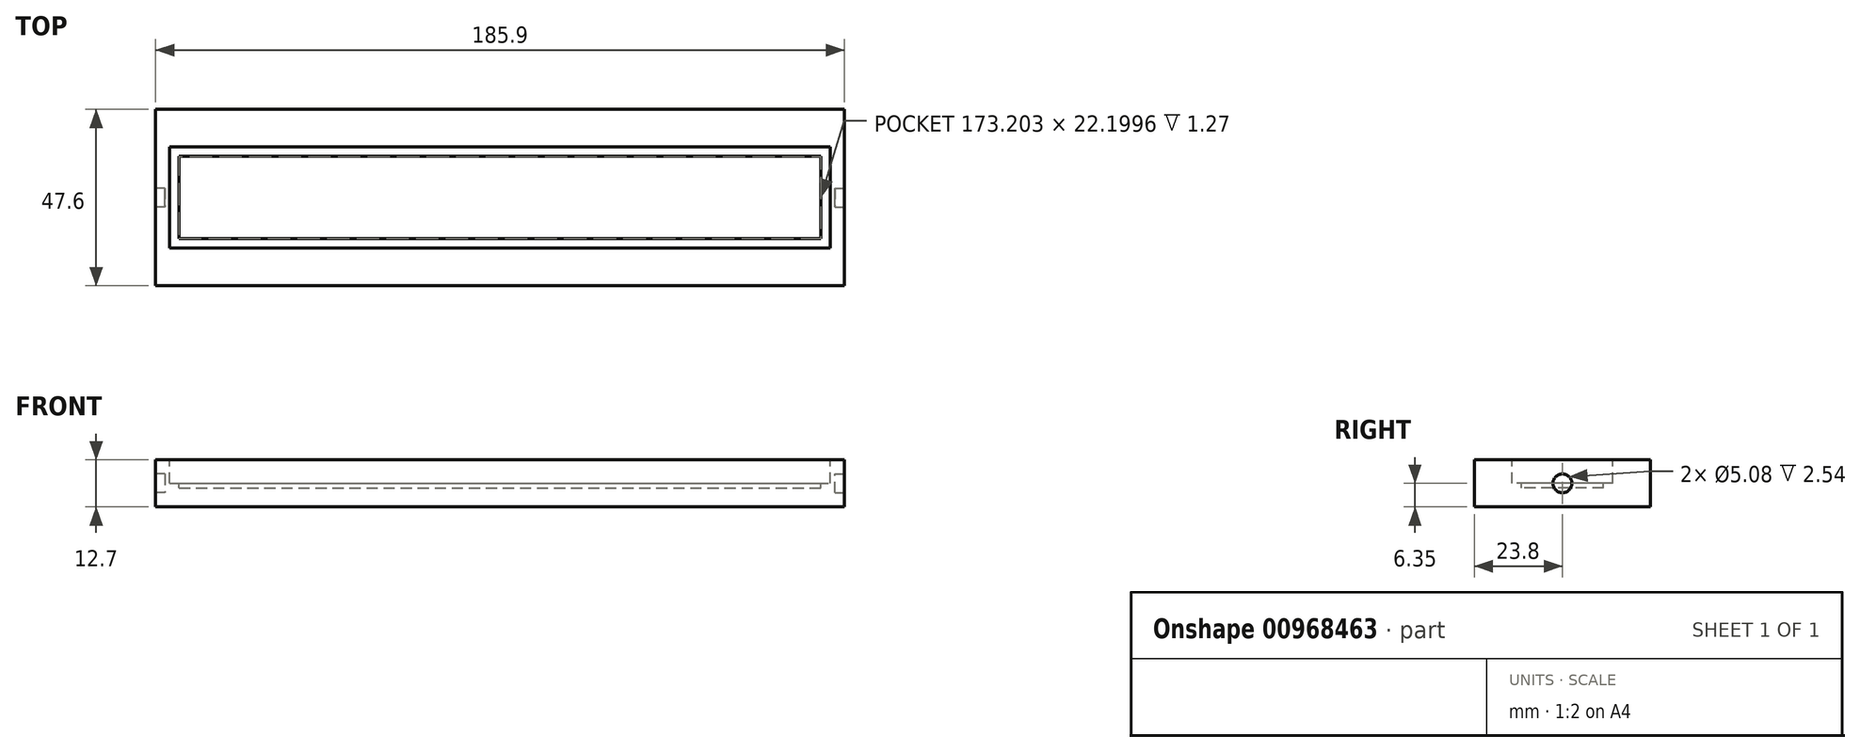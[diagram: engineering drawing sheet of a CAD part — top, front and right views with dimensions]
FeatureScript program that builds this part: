
annotation { "Feature Type Name" : "Feature", "Feature Type Description" : "" }
export const myFeature = defineFeature(function(context is Context, id is Id, definition is map)
    precondition{}
    {
        {
            var Q0;
            Q0=qCreatedBy(makeId("Top.planeOp"),FACE);
            var sketch = newSketch(context, id + "F0", { "sketchPlane" : qUnion([Q0])});
            skLineSegment(sketch, "E0.bottom", {"start": v(-92.95, 23.8) * mm, "end": v(92.95, 23.8) * mm});
            skLineSegment(sketch, "E0.top", {"start": v(-92.95, -23.8) * mm, "end": v(92.95, -23.8) * mm});
            skLineSegment(sketch, "E0.left", {"start": v(-92.95, 23.8) * mm, "end": v(-92.95, -23.8) * mm});
            skLineSegment(sketch, "E0.right", {"start": v(92.95, 23.8) * mm, "end": v(92.95, -23.8) * mm});
            skPoint(sketch, "E0.middle", {"position": v(0, 0) * mm});
            skSolve(sketch);
        }
        {
            var Q0;
            Q0=makeQuery(id+"F0.imprint","IMPRINT",FACE,{"disambiguationData":[TD([[makeQuery(id+"F0.imprint","IMPRINT",EDGE,{"derivedFrom":sQuery(id+"F0.wireOp",EDGE,"E0.bottom")}),-1.0]])]});
            extrude(context, id + "F1", {"entities" : qUnion([Q0]), "depth" : 12.7 * mm, "offsetDistance" : 25.4 * mm});
        }
        {
            var Q0;
            Q0=makeQuery(id+"F1.opExtrude","SWEPT_FACE",FACE,{"disambiguationData":[OSD([sQuery(id+"F0.wireOp",EDGE,"E0.right")])]});
            var sketch = newSketch(context, id + "F2", { "sketchPlane" : qUnion([Q0])});
            skCircle(sketch, "E1", {"center": v(0, 6.35) * mm, "radius": 2.54 * mm});
            skSolve(sketch);
        }
        {
            var Q0;
            Q0=makeQuery(id+"F2.imprint","IMPRINT",FACE,{"disambiguationData":[TD([[makeQuery(id+"F2.imprint","IMPRINT",EDGE,{"derivedFrom":sQuery(id+"F2.wireOp",EDGE,"E1")}),1.0]])]});
            extrude(context, id + "F3", {"entities" : qUnion([Q0]), "operationType" : NewBodyOperationType.REMOVE, "oppositeDirection" : true, "depth" : 2.54 * mm, "offsetDistance" : 25.4 * mm});
        }
        {
            var Q0;
            Q0=makeQuery(id+"F1.opExtrude","SWEPT_FACE",FACE,{"disambiguationData":[OSD([sQuery(id+"F0.wireOp",EDGE,"E0.left")])]});
            var sketch = newSketch(context, id + "F4", { "sketchPlane" : qUnion([Q0])});
            skCircle(sketch, "E2", {"center": v(0, 6.35) * mm, "radius": 2.54 * mm});
            skPoint(sketch, "E2.centerSnap0", {"position": v(23.8, 6.35) * mm});
            skSolve(sketch);
        }
        {
            var Q0;
            Q0=makeQuery(id+"F4.imprint","IMPRINT",FACE,{"disambiguationData":[TD([[makeQuery(id+"F4.imprint","IMPRINT",EDGE,{"derivedFrom":sQuery(id+"F4.wireOp",EDGE,"E2")}),1.0]])]});
            extrude(context, id + "F5", {"entities" : qUnion([Q0]), "operationType" : NewBodyOperationType.REMOVE, "oppositeDirection" : true, "depth" : 2.54 * mm, "offsetDistance" : 25.4 * mm});
        }
        {
            var Q0;
            Q0=makeQuery(id+"F1.opExtrude","CAP_FACE",FACE,{"disambiguationData":[OSD([sQuery(id+"F0.wireOp",EDGE,"E0.bottom"),sQuery(id+"F0.wireOp",EDGE,"E0.top"),sQuery(id+"F0.wireOp",EDGE,"E0.left"),sQuery(id+"F0.wireOp",EDGE,"E0.right")])],"isStart":false});
            var sketch = newSketch(context, id + "F6", { "sketchPlane" : qUnion([Q0])});
            skLineSegment(sketch, "E3.bottom", {"start": v(-86.6, 11.1) * mm, "end": v(86.6, 11.1) * mm});
            skLineSegment(sketch, "E3.top", {"start": v(-86.6, -11.1) * mm, "end": v(86.6, -11.1) * mm});
            skLineSegment(sketch, "E3.left", {"start": v(-86.6, 11.1) * mm, "end": v(-86.6, -11.1) * mm});
            skLineSegment(sketch, "E3.right", {"start": v(86.6, 11.1) * mm, "end": v(86.6, -11.1) * mm});
            skPoint(sketch, "E3.middle", {"position": v(0, 0) * mm});
            skSolve(sketch);
        }
        {
            var Q0;
            Q0=makeQuery(id+"F6.imprint","IMPRINT",FACE,{"disambiguationData":[TD([[makeQuery(id+"F6.imprint","IMPRINT",EDGE,{"derivedFrom":sQuery(id+"F6.wireOp",EDGE,"E3.bottom")}),-1.0]])]});
            extrude(context, id + "F7", {"entities" : qUnion([Q0]), "operationType" : NewBodyOperationType.REMOVE, "oppositeDirection" : true, "depth" : 7.62 * mm, "offsetDistance" : 25.4 * mm});
        }
        {
            var Q0;
            Q0=makeQuery(id+"F1.opExtrude","CAP_FACE",FACE,{"disambiguationData":[OSD([sQuery(id+"F0.wireOp",EDGE,"E0.bottom"),sQuery(id+"F0.wireOp",EDGE,"E0.top"),sQuery(id+"F0.wireOp",EDGE,"E0.left"),sQuery(id+"F0.wireOp",EDGE,"E0.right")])],"isStart":false});
            var sketch = newSketch(context, id + "F8", { "sketchPlane" : qUnion([Q0])});
            skLineSegment(sketch, "E4.bottom", {"start": v(-89.14, 13.64) * mm, "end": v(89.14, 13.64) * mm});
            skLineSegment(sketch, "E4.top", {"start": v(-89.14, -13.64) * mm, "end": v(89.14, -13.64) * mm});
            skLineSegment(sketch, "E4.left", {"start": v(-89.14, 13.64) * mm, "end": v(-89.14, -13.64) * mm});
            skLineSegment(sketch, "E4.right", {"start": v(89.14, 13.64) * mm, "end": v(89.14, -13.64) * mm});
            skPoint(sketch, "E4.middle", {"position": v(0, 0) * mm});
            skSolve(sketch);
        }
        {
            var Q0;
            Q0=makeQuery(id+"F8.imprint","IMPRINT",FACE,{"disambiguationData":[TD([[makeQuery(id+"F8.imprint","IMPRINT",EDGE,{"derivedFrom":sQuery(id+"F8.wireOp",EDGE,"E4.bottom")}),-1.0]])]});
            extrude(context, id + "F9", {"entities" : qUnion([Q0]), "operationType" : NewBodyOperationType.REMOVE, "oppositeDirection" : true, "depth" : 6.35 * mm, "offsetDistance" : 25.4 * mm});
        }
    });
